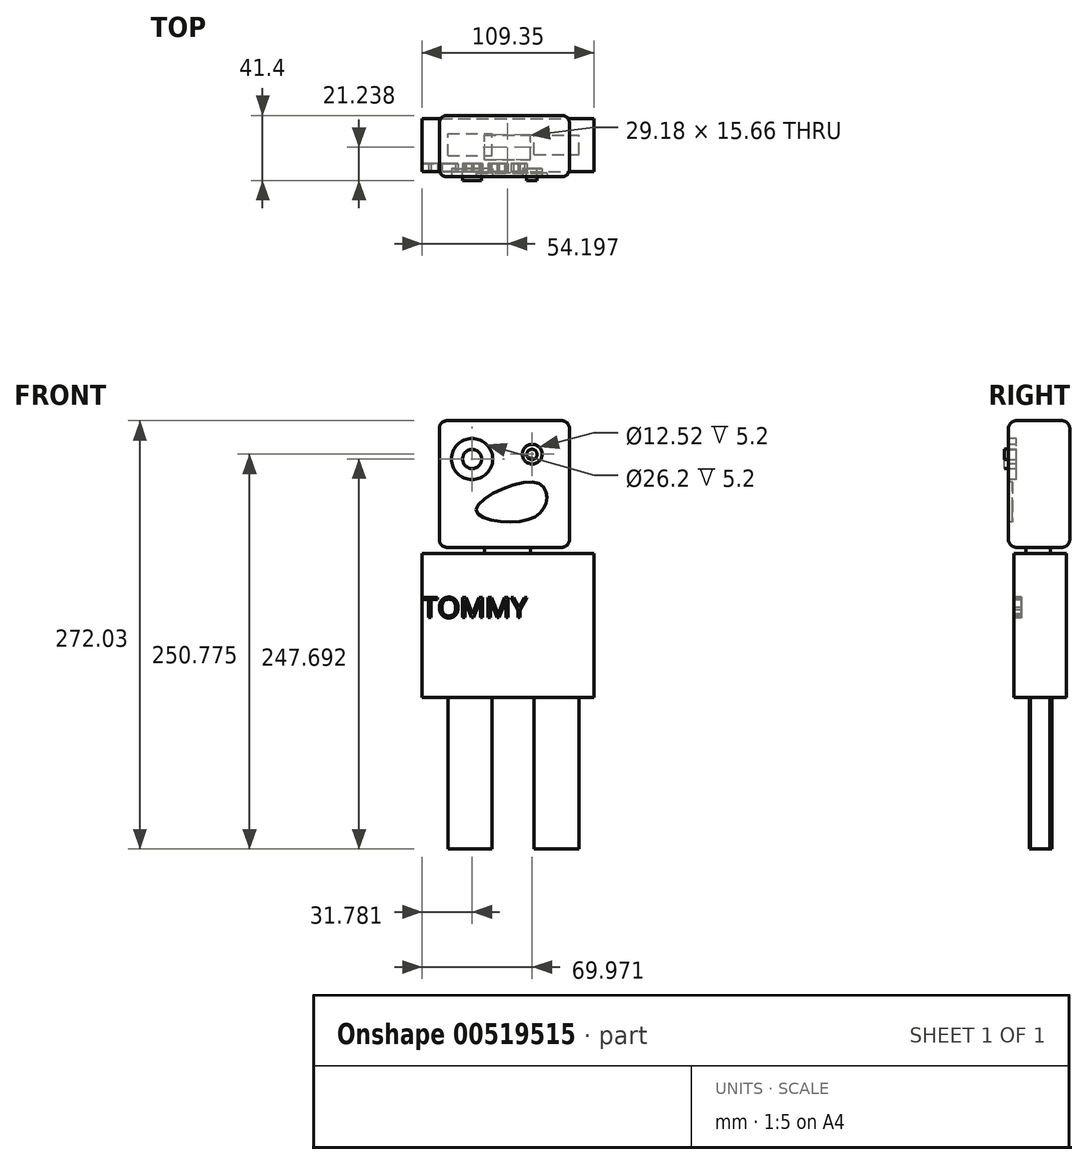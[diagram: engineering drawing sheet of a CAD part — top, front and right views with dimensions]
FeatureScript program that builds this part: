
annotation { "Feature Type Name" : "Feature", "Feature Type Description" : "" }
export const myFeature = defineFeature(function(context is Context, id is Id, definition is map)
    precondition{}
    {
        {
            var Q0;
            Q0=qCreatedBy(makeId("Front.planeOp"),FACE);
            var sketch = newSketch(context, id + "F0", { "sketchPlane" : qUnion([Q0])});
            skLineSegment(sketch, "E0.bottom", {"start": v(-100.44, 56.36) * mm, "end": v(-17.67, 56.36) * mm});
            skLineSegment(sketch, "E0.top", {"start": v(-100.44, -24.07) * mm, "end": v(-17.67, -24.07) * mm});
            skLineSegment(sketch, "E0.left", {"start": v(-100.44, 56.36) * mm, "end": v(-100.44, -24.07) * mm});
            skLineSegment(sketch, "E0.right", {"start": v(-17.67, 56.36) * mm, "end": v(-17.67, -24.07) * mm});
            skSolve(sketch);
        }
        {
            var Q0;
            Q0 = qSketchRegion(id + "F0", true);
            extrude(context, id + "F1", {"entities" : qUnion([Q0]), "depth" : 39 * mm, "offsetDistance" : 25 * mm});
        }
        {
            var Q0;
            Q0=makeQuery(id+"F1.opExtrude","CAP_EDGE",EDGE,{"disambiguationData":[OSD([sQuery(id+"F0.wireOp",EDGE,"E0.bottom")])],"isStart":false});
            var Q1;
            Q1=makeQuery(id+"F1.opExtrude","CAP_EDGE",EDGE,{"disambiguationData":[OSD([sQuery(id+"F0.wireOp",EDGE,"E0.left")])],"isStart":false});
            var Q2;
            Q2=makeQuery(id+"F1.opExtrude","SWEPT_EDGE",EDGE,{"disambiguationData":[OSD([sQuery(id+"F0.wireOp",EDGE,"E0.bottom"),sQuery(id+"F0.wireOp",EDGE,"E0.left")])]});
            var Q3;
            Q3=makeQuery(id+"F1.opExtrude","SWEPT_EDGE",EDGE,{"disambiguationData":[OSD([sQuery(id+"F0.wireOp",EDGE,"E0.top"),sQuery(id+"F0.wireOp",EDGE,"E0.left")])]});
            var Q4;
            Q4=makeQuery(id+"F1.opExtrude","CAP_EDGE",EDGE,{"disambiguationData":[OSD([sQuery(id+"F0.wireOp",EDGE,"E0.top")])],"isStart":false});
            var Q5;
            Q5=makeQuery(id+"F1.opExtrude","CAP_EDGE",EDGE,{"disambiguationData":[OSD([sQuery(id+"F0.wireOp",EDGE,"E0.right")])],"isStart":false});
            var Q6;
            Q6=makeQuery(id+"F1.opExtrude","SWEPT_EDGE",EDGE,{"disambiguationData":[OSD([sQuery(id+"F0.wireOp",EDGE,"E0.top"),sQuery(id+"F0.wireOp",EDGE,"E0.right")])]});
            var Q7;
            Q7=makeQuery(id+"F1.opExtrude","SWEPT_EDGE",EDGE,{"disambiguationData":[OSD([sQuery(id+"F0.wireOp",EDGE,"E0.bottom"),sQuery(id+"F0.wireOp",EDGE,"E0.right")])]});
            var Q8;
            Q8=makeQuery(id+"F1.opExtrude","CAP_EDGE",EDGE,{"disambiguationData":[OSD([sQuery(id+"F0.wireOp",EDGE,"E0.right")])],"isStart":true});
            var Q9;
            Q9=makeQuery(id+"F1.opExtrude","CAP_EDGE",EDGE,{"disambiguationData":[OSD([sQuery(id+"F0.wireOp",EDGE,"E0.bottom")])],"isStart":true});
            var Q10;
            Q10=makeQuery(id+"F1.opExtrude","CAP_EDGE",EDGE,{"disambiguationData":[OSD([sQuery(id+"F0.wireOp",EDGE,"E0.top")])],"isStart":true});
            var Q11;
            Q11=makeQuery(id+"F1.opExtrude","CAP_EDGE",EDGE,{"disambiguationData":[OSD([sQuery(id+"F0.wireOp",EDGE,"E0.left")])],"isStart":true});
            fillet(context, id + "F2", {"entities" : qUnion([Q0, Q1, Q2, Q3, Q4, Q5, Q6, Q7, Q8, Q9, Q10, Q11]), "radius" : 5 * mm, "tangentPropagation" : true, "allowEdgeOverflow" : false});
        }
        {
            var Q0;
            Q0=makeQuery(id+"F1.opExtrude","CAP_FACE",FACE,{"disambiguationData":[OSD([sQuery(id+"F0.wireOp",EDGE,"E0.bottom"),sQuery(id+"F0.wireOp",EDGE,"E0.top"),sQuery(id+"F0.wireOp",EDGE,"E0.left"),sQuery(id+"F0.wireOp",EDGE,"E0.right")])],"isStart":false});
            var sketch = newSketch(context, id + "F3", { "sketchPlane" : qUnion([Q0])});
            skCircle(sketch, "E1", {"center": v(-79.6, 32.02) * mm, "radius": 13.1 * mm});
            skCircle(sketch, "E2", {"center": v(-41.42, 35.1) * mm, "radius": 6.26 * mm});
            skSolve(sketch);
        }
        {
            var Q0;
            Q0 = qSketchRegion(id + "F3", true);
            extrude(context, id + "F4", {"entities" : qUnion([Q0]), "operationType" : NewBodyOperationType.REMOVE, "oppositeDirection" : true, "depth" : 5.2 * mm, "offsetDistance" : 25 * mm});
        }
        {
            var Q0;
            Q0=makeQuery(id+"F4.boolean.opBoolean","COPY",FACE,{"derivedFrom":makeQuery(id+"F4.opExtrude","CAP_FACE",FACE,{"disambiguationData":[OSD([sQuery(id+"F3.wireOp",EDGE,"E1")])],"isStart":false})});
            var sketch = newSketch(context, id + "F5", { "sketchPlane" : qUnion([Q0])});
            skCircle(sketch, "E3", {"center": v(-79.6, 32.02) * mm, "radius": 6.02 * mm});
            skCircle(sketch, "E4", {"center": v(-41.6, 34.95) * mm, "radius": 3.3 * mm});
            skSolve(sketch);
        }
        {
            var Q0;
            Q0 = qSketchRegion(id + "F5", true);
            extrude(context, id + "F6", {"entities" : qUnion([Q0]), "operationType" : NewBodyOperationType.ADD, "depth" : 7.6 * mm, "offsetDistance" : 25 * mm});
        }
        {
            var Q0;
            Q0=makeQuery(id+"F1.opExtrude","CAP_FACE",FACE,{"disambiguationData":[OSD([sQuery(id+"F0.wireOp",EDGE,"E0.bottom"),sQuery(id+"F0.wireOp",EDGE,"E0.top"),sQuery(id+"F0.wireOp",EDGE,"E0.left"),sQuery(id+"F0.wireOp",EDGE,"E0.right")])],"isStart":false});
            var sketch = newSketch(context, id + "F7", { "sketchPlane" : qUnion([Q0])});
            skFitSpline(sketch, "E5", {"points": [v(-77, 0) * mm, v(-39.76, 17.32) * mm, v(-32.4, 5.22) * mm, v(-47.59, -7.35) * mm, v(-77, 0) * mm]});
            skSolve(sketch);
        }
        {
            var Q0;
            Q0 = qSketchRegion(id + "F7", true);
            extrude(context, id + "F8", {"entities" : qUnion([Q0]), "operationType" : NewBodyOperationType.REMOVE, "oppositeDirection" : true, "depth" : 2.4 * mm, "offsetDistance" : 25 * mm});
        }
        {
            var Q0;
            Q0=makeQuery(id+"F1.opExtrude","SWEPT_FACE",FACE,{"disambiguationData":[OSD([sQuery(id+"F0.wireOp",EDGE,"E0.top")])]});
            var sketch = newSketch(context, id + "F9", { "sketchPlane" : qUnion([Q0])});
            skLineSegment(sketch, "E6.bottom", {"start": v(-71.78, 27.99) * mm, "end": v(-42.6, 27.99) * mm});
            skLineSegment(sketch, "E6.top", {"start": v(-71.78, 12.33) * mm, "end": v(-42.6, 12.33) * mm});
            skLineSegment(sketch, "E6.left", {"start": v(-71.78, 27.99) * mm, "end": v(-71.78, 12.33) * mm});
            skLineSegment(sketch, "E6.right", {"start": v(-42.6, 27.99) * mm, "end": v(-42.6, 12.33) * mm});
            skSolve(sketch);
        }
        {
            var Q0;
            Q0 = qSketchRegion(id + "F9", true);
            extrude(context, id + "F10", {"entities" : qUnion([Q0]), "operationType" : NewBodyOperationType.ADD, "depth" : 3.8 * mm, "offsetDistance" : 25 * mm});
        }
        {
            var Q0;
            Q0=makeQuery(id+"F10.opExtrude","CAP_FACE",FACE,{"disambiguationData":[OSD([sQuery(id+"F9.wireOp",EDGE,"E6.bottom"),sQuery(id+"F9.wireOp",EDGE,"E6.top"),sQuery(id+"F9.wireOp",EDGE,"E6.left"),sQuery(id+"F9.wireOp",EDGE,"E6.right")])],"isStart":false});
            var sketch = newSketch(context, id + "F11", { "sketchPlane" : qUnion([Q0])});
            skLineSegment(sketch, "E7.bottom", {"start": v(-111.4, 35.58) * mm, "end": v(-2.04, 35.58) * mm});
            skLineSegment(sketch, "E7.top", {"start": v(-111.4, 2.13) * mm, "end": v(-2.04, 2.13) * mm});
            skLineSegment(sketch, "E7.left", {"start": v(-111.4, 35.58) * mm, "end": v(-111.4, 2.13) * mm});
            skLineSegment(sketch, "E7.right", {"start": v(-2.04, 35.58) * mm, "end": v(-2.04, 2.13) * mm});
            skSolve(sketch);
        }
        {
            var Q0;
            Q0 = qSketchRegion(id + "F11", true);
            extrude(context, id + "F12", {"entities" : qUnion([Q0]), "operationType" : NewBodyOperationType.ADD, "depth" : 91.7 * mm, "offsetDistance" : 25 * mm});
        }
        {
            var Q0;
            Q0=makeQuery(id+"F12.opExtrude","CAP_FACE",FACE,{"disambiguationData":[OSD([sQuery(id+"F11.wireOp",EDGE,"E7.bottom"),sQuery(id+"F11.wireOp",EDGE,"E7.top"),sQuery(id+"F11.wireOp",EDGE,"E7.left"),sQuery(id+"F11.wireOp",EDGE,"E7.right")])],"isStart":false});
            var sketch = newSketch(context, id + "F13", { "sketchPlane" : qUnion([Q0])});
            skLineSegment(sketch, "E8.bottom", {"start": v(-95.05, 25.62) * mm, "end": v(-67.06, 25.62) * mm});
            skLineSegment(sketch, "E8.top", {"start": v(-95.05, 11.39) * mm, "end": v(-67.06, 11.39) * mm});
            skLineSegment(sketch, "E8.left", {"start": v(-95.05, 25.62) * mm, "end": v(-95.05, 11.39) * mm});
            skLineSegment(sketch, "E8.right", {"start": v(-67.06, 25.62) * mm, "end": v(-67.06, 11.39) * mm});
            skLineSegment(sketch, "E9.bottom", {"start": v(-40.26, 24.9) * mm, "end": v(-11.8, 24.9) * mm});
            skLineSegment(sketch, "E9.top", {"start": v(-40.26, 12.57) * mm, "end": v(-11.8, 12.57) * mm});
            skLineSegment(sketch, "E9.left", {"start": v(-40.26, 24.9) * mm, "end": v(-40.26, 12.57) * mm});
            skLineSegment(sketch, "E9.right", {"start": v(-11.8, 24.9) * mm, "end": v(-11.8, 12.57) * mm});
            skSolve(sketch);
        }
        {
            var Q0;
            Q0 = qSketchRegion(id + "F13", true);
            extrude(context, id + "F14", {"entities" : qUnion([Q0]), "operationType" : NewBodyOperationType.ADD, "depth" : 96.1 * mm, "offsetDistance" : 25 * mm});
        }
        {
            var Q0;
            Q0=makeQuery(id+"F12.opExtrude","SWEPT_FACE",FACE,{"disambiguationData":[OSD([sQuery(id+"F11.wireOp",EDGE,"E7.bottom")])]});
            var sketch = newSketch(context, id + "F15", { "sketchPlane" : qUnion([Q0])});
            skText(sketch, "E10", { "text": "TOMMY", "fontName": "OpenSans-Regular.ttf"});
            const initialGuessF15  = {"E10": [-0.1114, -0.06875, 1, 0, 0.01297]};
            skSetInitialGuess(sketch, initialGuessF15);
            skSolve(sketch);
        }
        {
            var Q0;
            Q0 = qSketchRegion(id + "F15", true);
            extrude(context, id + "F16", {"entities" : qUnion([Q0]), "operationType" : NewBodyOperationType.REMOVE, "oppositeDirection" : true, "depth" : 5 * mm, "offsetDistance" : 25 * mm});
        }
    });
